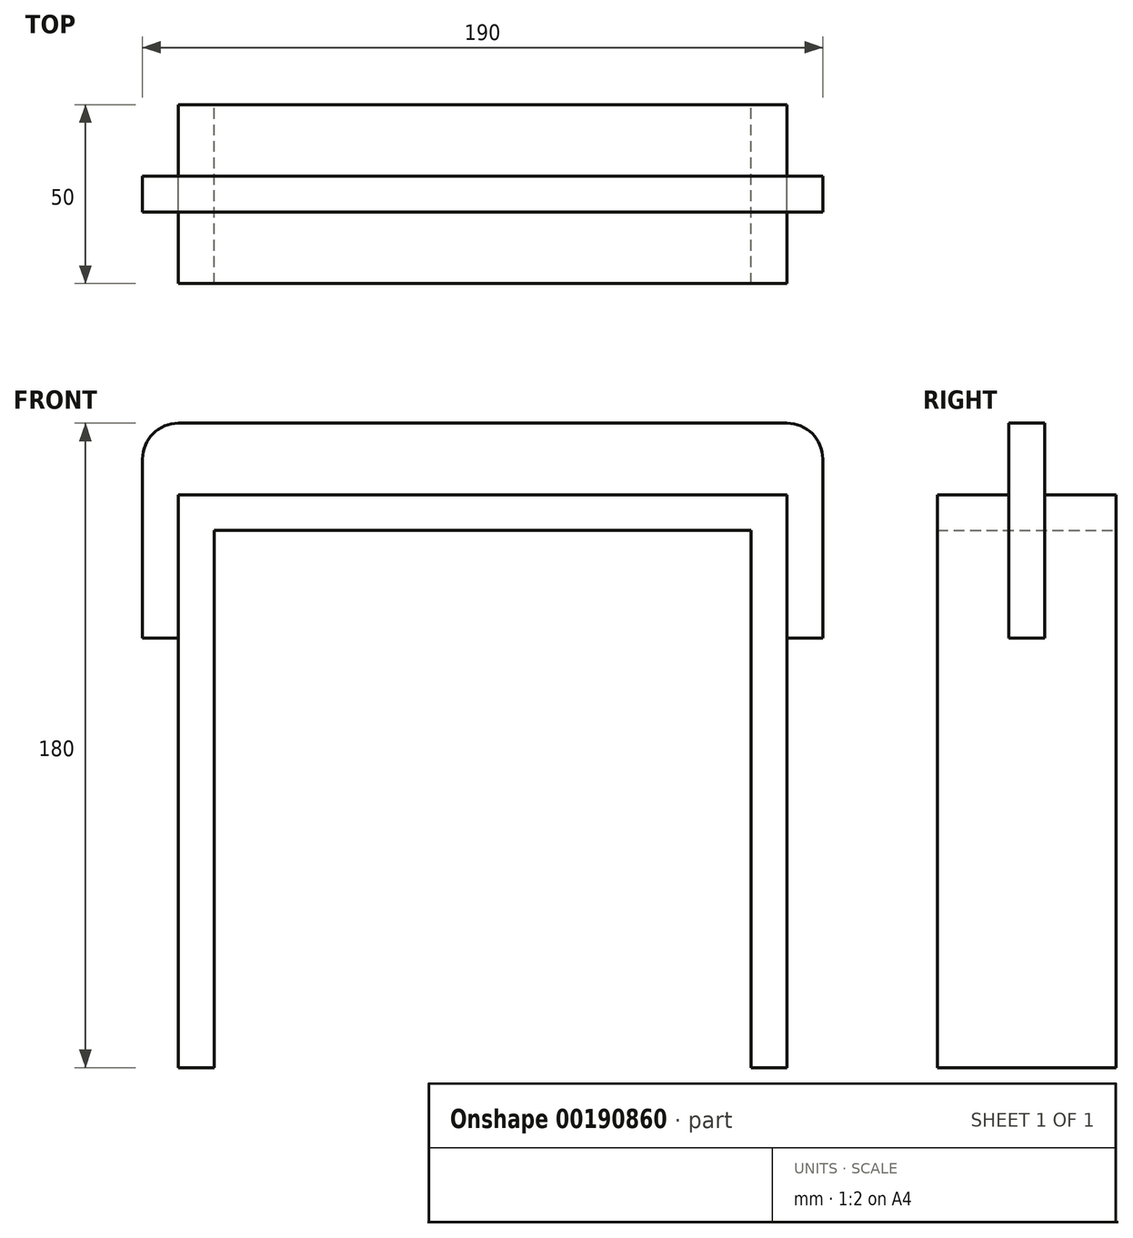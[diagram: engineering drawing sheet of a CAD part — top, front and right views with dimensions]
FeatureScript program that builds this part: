
annotation { "Feature Type Name" : "Feature", "Feature Type Description" : "" }
export const myFeature = defineFeature(function(context is Context, id is Id, definition is map)
    precondition{}
    {
        {
            var Q0;
            Q0=qCreatedBy(makeId("Front.planeOp"),FACE);
            var sketch = newSketch(context, id + "F0", { "sketchPlane" : qUnion([Q0])});
            skLineSegment(sketch, "E0", {"start": v(-85, -116.95) * mm, "end": v(-85, 43.05) * mm});
            skLineSegment(sketch, "E1", {"start": v(-85, 43.05) * mm, "end": v(85, 43.05) * mm});
            skLineSegment(sketch, "E2", {"start": v(85, 43.05) * mm, "end": v(85, -116.95) * mm});
            skLineSegment(sketch, "E3", {"start": v(85, -116.95) * mm, "end": v(75, -116.95) * mm});
            skLineSegment(sketch, "E4", {"start": v(75, -116.95) * mm, "end": v(75, 33.05) * mm});
            skLineSegment(sketch, "E5", {"start": v(75, 33.05) * mm, "end": v(-75, 33.05) * mm});
            skLineSegment(sketch, "E6", {"start": v(-75, 33.05) * mm, "end": v(-75, -116.95) * mm});
            skLineSegment(sketch, "E7", {"start": v(-75, -116.95) * mm, "end": v(-85, -116.95) * mm});
            skLineSegment(sketch, "E8", {"start": v(-85, 3.05) * mm, "end": v(-95, 3.05) * mm});
            skLineSegment(sketch, "E9", {"start": v(-95, 3.05) * mm, "end": v(-95, 53.05) * mm});
            skLineSegment(sketch, "E10", {"start": v(-85, 63.05) * mm, "end": v(85, 63.05) * mm});
            skLineSegment(sketch, "E11", {"start": v(95, 53.05) * mm, "end": v(95, 3.05) * mm});
            skLineSegment(sketch, "E12", {"start": v(95, 3.05) * mm, "end": v(85, 3.05) * mm});
            skPoint(sketch, "E13.visualSharp", {"position": v(-95, 63.05) * mm});
            skArc(sketch, "E13.filletArc", {"start": v(-85, 63.05) * mm, "mid": v(-92.07, 60.12) * mm, "end": v(-95, 53.05) * mm});
            skPoint(sketch, "E14.visualSharp", {"position": v(95, 63.05) * mm});
            skArc(sketch, "E14.filletArc", {"start": v(95, 53.05) * mm, "mid": v(92.07, 60.12) * mm, "end": v(85, 63.05) * mm});
            skSolve(sketch);
        }
        {
            var Q0;
            {var subQ1=sQuery(id+"F0.wireOp",EDGE,"E1");Q0=makeQuery(id+"F0.imprint","IMPRINT",FACE,{"disambiguationData":[TD([[makeQuery(id+"F0.imprint","IMPRINT",EDGE,{"derivedFrom":subQ1}),-1.0]])]});}
            extrude(context, id + "F1", {"entities" : qUnion([Q0]), "depth" : 50 * mm, "symmetric" : true});
        }
        {
            var Q0;
            Q0 = qSketchRegion(id + "F0", true);
            extrude(context, id + "F2", {"entities" : qUnion([Q0]), "operationType" : NewBodyOperationType.ADD, "depth" : 10 * mm, "symmetric" : true});
        }
    });
